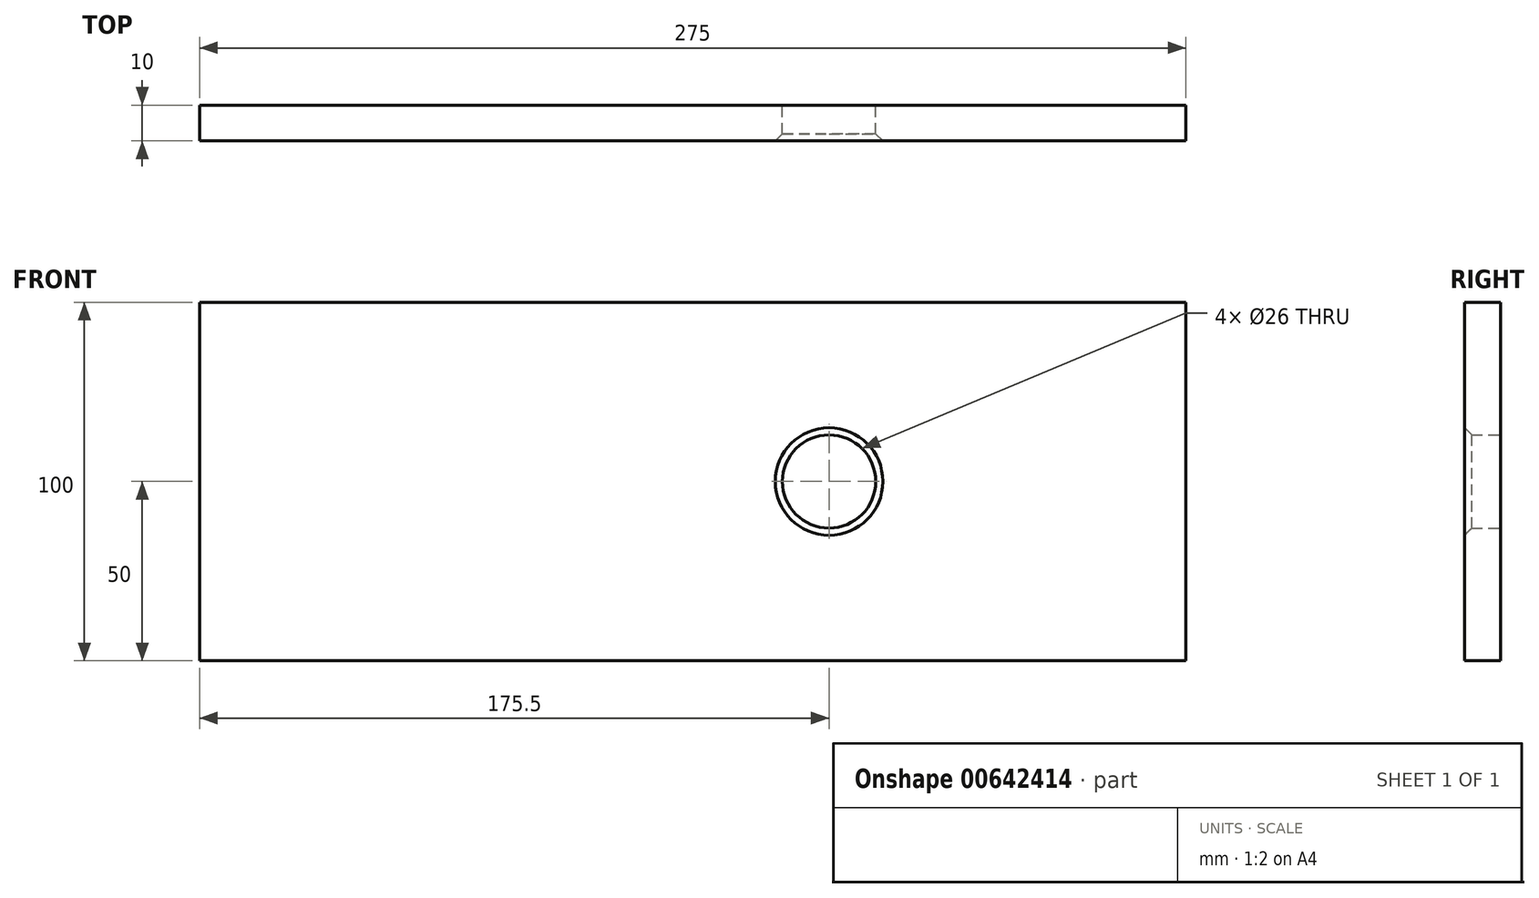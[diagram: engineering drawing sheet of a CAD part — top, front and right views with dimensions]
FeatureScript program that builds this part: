
annotation { "Feature Type Name" : "Feature", "Feature Type Description" : "" }
export const myFeature = defineFeature(function(context is Context, id is Id, definition is map)
    precondition{}
    {
        {
            var Q0;
            Q0=qCreatedBy(makeId("Front.planeOp"),FACE);
            var sketch = newSketch(context, id + "F0", { "sketchPlane" : qUnion([Q0])});
            skLineSegment(sketch, "E0.bottom", {"start": v(137.5, -50) * mm, "end": v(-137.5, -50) * mm});
            skLineSegment(sketch, "E0.top", {"start": v(137.5, 50) * mm, "end": v(-137.5, 50) * mm});
            skLineSegment(sketch, "E0.left", {"start": v(137.5, -50) * mm, "end": v(137.5, 50) * mm});
            skLineSegment(sketch, "E0.right", {"start": v(-137.5, -50) * mm, "end": v(-137.5, 50) * mm});
            skPoint(sketch, "E0.middle", {"position": v(0, 0) * mm});
            skCircle(sketch, "E1", {"center": v(38, 0) * mm, "radius": 13 * mm});
            skSolve(sketch);
        }
        {
            var Q0;
            Q0=makeQuery(id+"F0.imprint","IMPRINT",FACE,{"disambiguationData":[TD([[makeQuery(id+"F0.imprint","IMPRINT",EDGE,{"derivedFrom":sQuery(id+"F0.wireOp",EDGE,"E0.bottom")}),-1.0]])]});
            extrude(context, id + "F1", {"entities" : qUnion([Q0]), "depth" : 10 * mm, "offsetDistance" : 25 * mm});
        }
        {
            var Q0;
            Q0=makeQuery(id+"F1.opExtrude","CAP_EDGE",EDGE,{"disambiguationData":[OSD([sQuery(id+"F0.wireOp",EDGE,"E1")])],"isStart":false});
            chamfer(context, id + "F2", {"entities" : qUnion([Q0]), "width" : 2 * mm, "tangentPropagation" : true});
        }
    });
